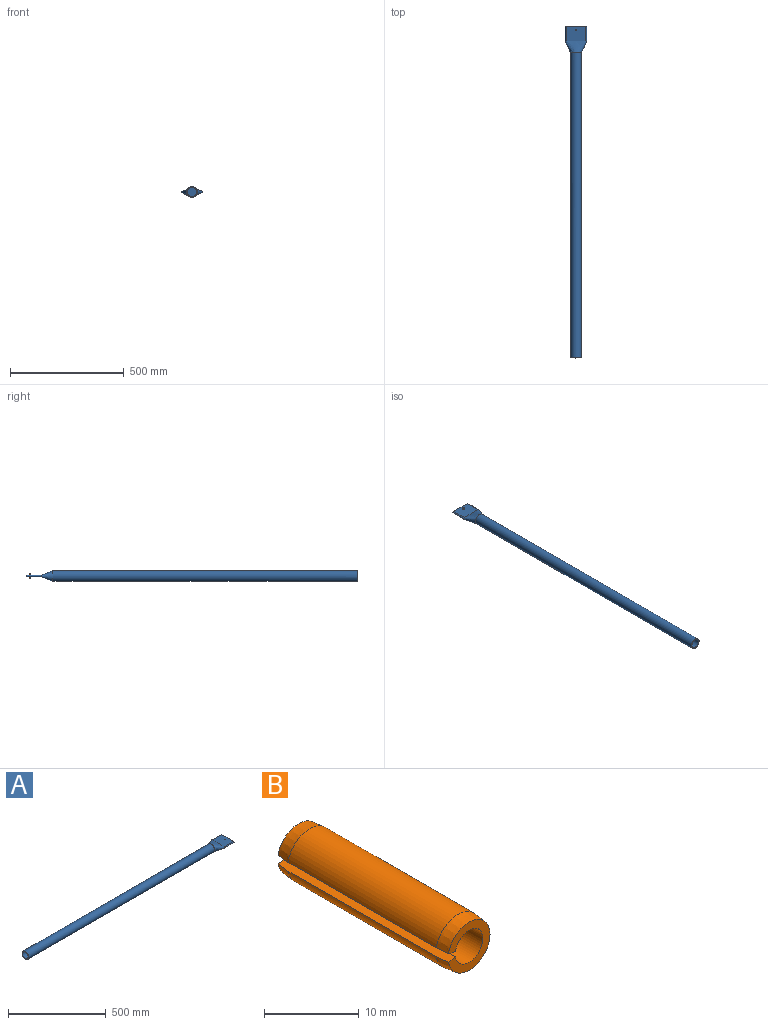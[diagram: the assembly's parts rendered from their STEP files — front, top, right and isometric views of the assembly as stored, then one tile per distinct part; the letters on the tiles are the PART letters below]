
ASSEMBLY  parts=2 mates=1
PART A: 18 faces, bbox 1494.4x126.2x81.3 mm
  f0: plane 48.27x48.27mm, normal (-1,0,0), area 532.1mm2, adj f1,f10
  f1: cylinder r=20.32mm len=1343.48mm, axis (1,0,0), area 171353.5mm2, adj f0,f2,f3,f4,f5,f6,f7,f8
  f2: offset ~57.11x21.36mm, area 17.6mm2, adj f1,f3
  f3: plane 73.55x72.91mm, normal (-1,0,0), area 1289.5mm2, adj f1,f2,f4
  f4: offset ~58.37x33.32mm, area 11.6mm2, adj f1,f3
  f5: cylinder r=3.38mm len=6.76mm, axis (0,0,-1), area 80.9mm2, adj f1,f10
  f6: cylinder r=3.38mm len=6.76mm, axis (0,0,-1), area 80.9mm2, adj f1,f10
  f7: cylinder r=3.38mm len=6.76mm, axis (0,0,-1), area 80.9mm2, adj f1,f10
  f8: cylinder r=3.38mm len=6.76mm, axis (0,0,-1), area 80.9mm2, adj f1,f10
  f9: cylinder r=3.38mm len=6.76mm, axis (0,0,-1), area 80.9mm2, adj f1,f10
  f10: cylinder r=24.13mm len=1343.48mm, axis (1,0,0), area 203541.3mm2, adj f0,f5,f6,f7,f8,f9,f11
  f11: bspline ~93.24x50.88mm, area 9083.4mm2, adj f10,f12,f15,f16,f17
  f12: plane 85.63x67.18mm, normal (0,0,-1), area 5720.8mm2, adj f11,f13,f14,f15,f17
  f13: cylinder r=3.17mm len=7.62mm, axis (0,0,-1), area 152mm2, adj f12,f16
  f14: plane 93.25x7.62mm, normal (1,0,0), area 698.1mm2, adj f12,f15,f16,f17
  f15: cylinder r=3.81mm len=67.18mm, axis (1,0,0), area 804.1mm2, adj f11,f12,f14,f16
  f16: plane 90.7x72.24mm, normal (0,0,1), area 5720.8mm2, adj f11,f13,f14,f15,f17
  f17: cylinder r=3.81mm len=67.18mm, axis (1,0,0), area 804.1mm2, adj f11,f12,f14,f16
PART B: 8 faces, bbox 6.5x25.4x6.6 mm
  f0: cone r=3.28mm half-angle=5.7deg, axis (0,-1,0), area 31.4mm2, adj f2,f3,f4,f6
  f1: cylinder r=2.06mm len=25.4mm, axis (0,1,0), area 310.1mm2, adj f2,f4,f5,f6
  f2: plane 25.4x1.2mm, normal (-0.17,0,0.98), area 30.7mm2, adj f0,f1,f3,f5,f6,f7
  f3: cylinder r=3.28mm len=22.1mm, axis (0,1,0), area 429.7mm2, adj f0,f2,f4,f7
  f4: plane 25.4x1.2mm, normal (-0.17,0,-0.98), area 30.7mm2, adj f0,f1,f3,f5,f6,f7
  f5: plane 6.22x6.18mm, normal (0,-1,0), area 16.2mm2, adj f1,f2,f4,f7
  f6: plane 6.22x6.18mm, normal (0,1,0), area 16.2mm2, adj f0,f1,f2,f4
  f7: cone r=3.11mm half-angle=5.7deg, axis (0,1,0), area 31.4mm2, adj f2,f3,f4,f5
PLACE A rot(axis=(0,0,1),90deg) t=(1005.37,2035.37,3531.33)mm
PLACE B rot(axis=(1,0,0),90deg) t=(1005.37,3646.97,3531.33)mm
MATE fastened B.f1 <-> A.f13  axis (0,0,1) through (1005.37,3646.97,3531.33)mm
